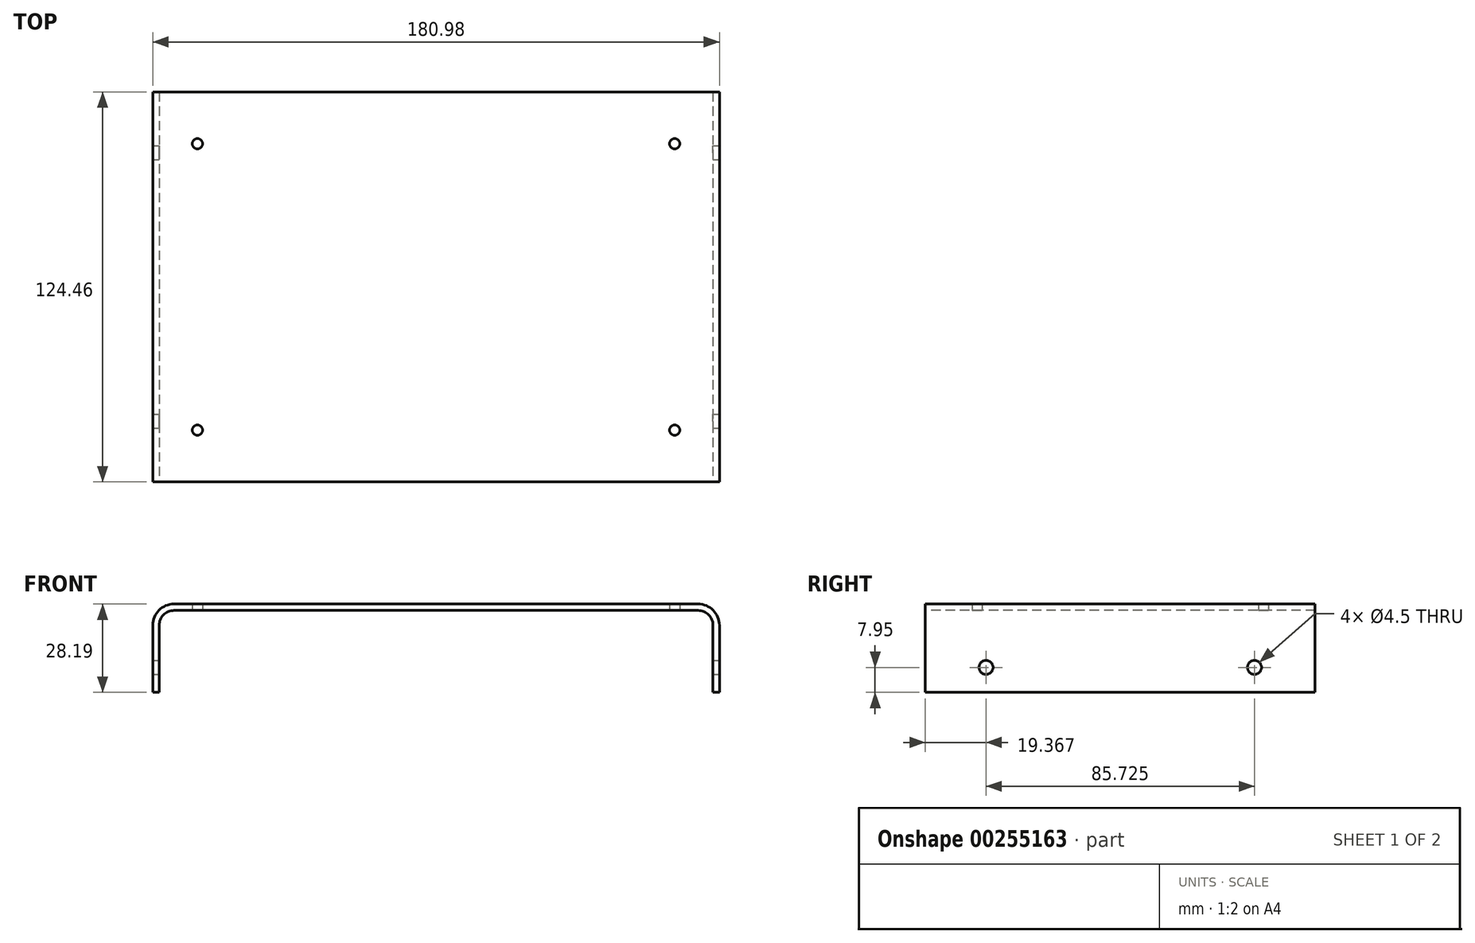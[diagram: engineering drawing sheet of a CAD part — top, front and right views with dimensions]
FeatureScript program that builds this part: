
annotation { "Feature Type Name" : "Feature", "Feature Type Description" : "" }
export const myFeature = defineFeature(function(context is Context, id is Id, definition is map)
    precondition{}
    {
        {
            var Q0;
            Q0=qCreatedBy(makeId("Front.planeOp"),FACE);
            var sketch = newSketch(context, id + "F0", { "sketchPlane" : qUnion([Q0])});
            skLineSegment(sketch, "E0", {"start": v(0, 0) * mm, "end": v(0, 21.36) * mm});
            skLineSegment(sketch, "E1", {"start": v(6.83, 28.2) * mm, "end": v(174.14, 28.2) * mm});
            skLineSegment(sketch, "E2", {"start": v(180.97, 21.36) * mm, "end": v(180.97, 0) * mm});
            skPoint(sketch, "E3.visualSharp", {"position": v(0, 28.2) * mm});
            skArc(sketch, "E3.filletArc", {"start": v(6.83, 28.2) * mm, "mid": v(2, 26.2) * mm, "end": v(0, 21.36) * mm});
            skPoint(sketch, "E4.visualSharp", {"position": v(180.98, 28.2) * mm});
            skArc(sketch, "E4.filletArc", {"start": v(180.97, 21.36) * mm, "mid": v(178.97, 26.2) * mm, "end": v(174.14, 28.2) * mm});
            skLineSegment(sketch, "E5.0", {"start": v(178.92, 21.36) * mm, "end": v(178.92, 0) * mm});
            skLineSegment(sketch, "E5.1", {"start": v(2.06, 0) * mm, "end": v(2.06, 21.36) * mm});
            skArc(sketch, "E5.2", {"start": v(6.83, 26.14) * mm, "mid": v(3.46, 24.74) * mm, "end": v(2.06, 21.36) * mm});
            skLineSegment(sketch, "E5.3", {"start": v(6.83, 26.14) * mm, "end": v(174.14, 26.14) * mm});
            skArc(sketch, "E5.4", {"start": v(178.92, 21.36) * mm, "mid": v(177.52, 24.74) * mm, "end": v(174.14, 26.14) * mm});
            skLineSegment(sketch, "E6", {"start": v(2.06, 0) * mm, "end": v(0, 0) * mm});
            skLineSegment(sketch, "E7", {"start": v(180.97, 0) * mm, "end": v(178.92, 0) * mm});
            skSolve(sketch);
        }
        {
            var Q0;
            Q0=makeQuery(id+"F0.imprint","IMPRINT",FACE,{"disambiguationData":[TD([[makeQuery(id+"F0.imprint","IMPRINT",EDGE,{"derivedFrom":sQuery(id+"F0.wireOp",EDGE,"E0")}),-1.0]])]});
            extrude(context, id + "F1", {"entities" : qUnion([Q0]), "oppositeDirection" : true, "depth" : 124.46 * mm});
        }
        {
            var Q0;
            Q0=makeQuery(id+"F1.opExtrude","SWEPT_FACE",FACE,{"disambiguationData":[OSD([sQuery(id+"F0.wireOp",EDGE,"E2")])]});
            var sketch = newSketch(context, id + "F2", { "sketchPlane" : qUnion([Q0])});
            skPoint(sketch, "E8", {"position": v(19.37, 7.95) * mm});
            skPoint(sketch, "E9", {"position": v(105.1, 7.95) * mm});
            skSolve(sketch);
        }
        {
            var Q0;
            Q0=sQuery(id+"F2.wireOp",VERTEX,"E8");
            var Q1;
            Q1=sQuery(id+"F2.wireOp",VERTEX,"E9");
            var Q2;
            Q2=makeQuery(id+"F1.opExtrude","SWEPT_BODY",BODY,{"disambiguationData":[OSD([sQuery(id+"F0.wireOp",EDGE,"E0"),sQuery(id+"F0.wireOp",EDGE,"E1"),sQuery(id+"F0.wireOp",EDGE,"E2"),sQuery(id+"F0.wireOp",EDGE,"E3.filletArc"),sQuery(id+"F0.wireOp",EDGE,"E4.filletArc"),sQuery(id+"F0.wireOp",EDGE,"E5.0"),sQuery(id+"F0.wireOp",EDGE,"E5.1"),sQuery(id+"F0.wireOp",EDGE,"E5.2"),sQuery(id+"F0.wireOp",EDGE,"E5.3"),sQuery(id+"F0.wireOp",EDGE,"E5.4"),sQuery(id+"F0.wireOp",EDGE,"E6"),sQuery(id+"F0.wireOp",EDGE,"E7")])]});
            hole(context, id + "F3", {"style" : HoleStyle.SIMPLE, "endStyle" : HoleEndStyle.THROUGH, "holeDiameter" : 4.5 * mm, "tappedDepth" : 12.7 * mm, "tapClearance" : 3, "locations" : qUnion([Q0, Q1]), "scope" : qUnion([Q2])});
        }
        {
            var Q0;
            Q0=makeQuery(id+"F1.opExtrude","SWEPT_FACE",FACE,{"disambiguationData":[OSD([sQuery(id+"F0.wireOp",EDGE,"E5.3")])]});
            var sketch = newSketch(context, id + "F4", { "sketchPlane" : qUnion([Q0])});
            skPoint(sketch, "E10", {"position": v(14.29, -16.51) * mm});
            skPoint(sketch, "E11", {"position": v(166.69, -16.5) * mm});
            skPoint(sketch, "E12", {"position": v(166.69, -107.95) * mm});
            skPoint(sketch, "E13", {"position": v(14.29, -107.95) * mm});
            skSolve(sketch);
        }
        {
            var Q0;
            Q0=sQuery(id+"F4.wireOp",VERTEX,"E10");
            var Q1;
            Q1=sQuery(id+"F4.wireOp",VERTEX,"E13");
            var Q2;
            Q2=sQuery(id+"F4.wireOp",VERTEX,"E11");
            var Q3;
            Q3=sQuery(id+"F4.wireOp",VERTEX,"E12");
            var Q4;
            Q4=makeQuery(id+"F1.opExtrude","SWEPT_BODY",BODY,{"disambiguationData":[OSD([sQuery(id+"F0.wireOp",EDGE,"E0"),sQuery(id+"F0.wireOp",EDGE,"E1"),sQuery(id+"F0.wireOp",EDGE,"E2"),sQuery(id+"F0.wireOp",EDGE,"E3.filletArc"),sQuery(id+"F0.wireOp",EDGE,"E4.filletArc"),sQuery(id+"F0.wireOp",EDGE,"E5.0"),sQuery(id+"F0.wireOp",EDGE,"E5.1"),sQuery(id+"F0.wireOp",EDGE,"E5.2"),sQuery(id+"F0.wireOp",EDGE,"E5.3"),sQuery(id+"F0.wireOp",EDGE,"E5.4"),sQuery(id+"F0.wireOp",EDGE,"E6"),sQuery(id+"F0.wireOp",EDGE,"E7")])]});
            hole(context, id + "F5", {"style" : HoleStyle.SIMPLE, "endStyle" : HoleEndStyle.THROUGH, "standardTappedOrClearance" : lookupTablePath({ "standard" : "ANSI", "fit" : "Normal (ASME)", "size" : "#4", "type" : "Clearance" }), "standardBlindInLast" : lookupTablePath({ "fit" : "Free", "standard" : "ANSI", "size" : "#4", "type" : "Clearance" }), "holeDiameter" : 3.26 * mm, "tappedDepth" : 2.77 * mm, "tapClearance" : 3, "startFromSketch" : true, "locations" : qUnion([Q0, Q1, Q2, Q3]), "scope" : qUnion([Q4]), "majorDiameter" : 6.35 * mm});
        }
    });
